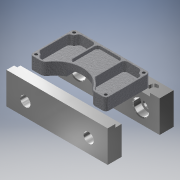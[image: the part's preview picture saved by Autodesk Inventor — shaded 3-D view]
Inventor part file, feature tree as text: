
AUTODESK INVENTOR PART (.ipt)
format: ipt  version: 2017 (Build 210142000, 142)  size: 843,264 bytes
history: native  units: in
note: dims shown in document units (in); Inventor stores cm internally (conversion verified against a paired STEP export)
features: extrude x10, sketch x9, other x5, chamfer x5, hole x3, plane x2, pattern_linear x1
ambient origin geometry x8: Origin, YZ Plane, XZ Plane, XY Plane, X Axis, Y Axis, Z Axis, Center Point
bodies: Body1 (feature_tree), Body2 (feature_tree), Body3 (feature_tree), Body4 (feature_tree), Body5 (feature_tree)
feature tree (35):
  other  "Model"
  extrude  "Extrusion1"  Depth=1.75in
  extrude  "Extrusion2"  Depth=1.075in
  sketch  "Sketch3"  dims[d5=0.125in d6=0.25in]
  extrude  "Extrusion3"  Depth=0.25in
  extrude  "Extrusion4"  Depth=0.25in
  chamfer  "Chamfer2"  Distance=0.25in
  hole  "Hole2"  [1 undecoded]
  chamfer  "Chamfer3"  Distance=0.375in
  pattern_linear  "Rectangular Pattern1"  Spacing1=1.0in  [1 undecoded]
  chamfer  "Chamfer1"  Distance=0.125in Angle=45.0deg
  plane  "Work Plane1"
  extrude  "Extrusion5"  Depth=1.5in
  plane  "Work Plane2"
  extrude  "Extrusion6"  Depth=1.5in
  extrude  "Extrusion7"  Depth=3.25in
  hole  "Hole4"  [1 undecoded]
  chamfer  "Chamfer4"  Distance=0.125in
  extrude  "Extrusion8"  Depth=0.125in
  hole  "Hole5"  [1 undecoded]
  chamfer  "Chamfer5"  Distance=0.375in
  extrude  "Extrusion9"  Depth=1.5in
  extrude  "Extrusion10"  Depth=1.5in
  sketch  "Sketch1"  dims[d0=1.75in d1=3.0in]
  sketch  "Sketch2"  dims[d3=0.5in d4=1.075in]
  sketch  "Sketch4"  dims[d7=0.5in d8=0.0in d10=1.0in d11=0.25in d12=0.0in]
  other  "Stock"
  other  "Vise Jaw - Fixed"
  sketch  "Sketch6"  dims[d13=0.063in d14=0.063in d15=0.375in d16=0.0in]
  sketch  "Sketch7"  dims[d17=0.125in d18=0.0in]
  other  "Vise Jaw"
  sketch  "Sketch8"  dims[d19=0.01in d20=0.125in d21=45.0deg]
  sketch  "Sketch9"  dims[d22=0.01in d23=0.125in d24=45.0deg]
  other  "Setup 2 - Stock"
  sketch  "Sketch10"  dims[d136=1.0in d137=1.0in d36=0.104in d37=0.25in d38=0.375in d39=0.25in d40=0.5635in d41=0.25in d42=0.0in d43=1.0in d44=1.0in d45=0.107in d46=0.25in d47=0.375in d48=0.25in d49=0.5635in d50=0.0938in d51=0.8108in d52=0.01in d53=0.125in d54=45.0deg d55=0.7874in d57=2.75in d58=0.7874in d60=1.5in d61=0.05in d62=3.25in d63=2.0in d64=0.125in d65=0.125in d66=0.75in d67=0.0in d68=0.375in d69=0.55in d70=1.25in d71=0.125in d72=0.25in d73=4.0in d74=0.0in d75=3.25in d76=0.375in d77=0.25in d78=0.14in d79=0.14in d80=0.3in d81=0.125in d82=0.0in d83=0.75in d84=2.5in d85=0.55in d86=0.4in d87=0.75in d88=0.6in d89=0.3in d90=0.5635in d91=1.0in d92=0.8108in d93=0.0312in d94=0.125in d95=45.0deg d96=1.25in d97=0.55in d100=4.0in d101=0.0in d102=0.75in d103=2.5in d104=0.55in d105=0.4in d106=0.75in d107=0.6in d108=0.3in d109=0.5635in d110=1.0in d111=0.8108in d112=0.0312in d113=0.125in d114=45.0deg d115=3.25in d116=2.0in d117=0.195in d118=0.0in d119=1.75in d120=3.0in d121=0.125in d122=0.125in d123=0.575in d124=1.075in d125=0.125in d126=0.25in d127=0.505in d128=0.0in d150=1.0in d151=1.0in d166=0.063in d167=0.0623in d168=0.063in d169=0.125in d170=0.125in d171=0.125in d172=0.1223in d173=0.1336in d174=0.1336in d175=0.125in d176=0.063in d177=0.063in d179=0.063in d180=0.071in d181=0.0751in d182=0.0713in d183=0.125in d184=1.0in d185=0.8673in d188=0.1253in d190=0.135in d191=0.125in d192=0.135in d193=0.135in d194=0.135in d195=0.135in d196=0.135in d197=0.135in d198=0.125in d199=0.135in d201=0.135in d204=0.063in d205=1.5in d206=0.135in d207=0.135in d208=0.135in d209=0.135in d210=1.5in d25=1.0in d26=1.0in d34=1.0in d35=1.0in]
note: 4 required parameter values undecoded (feature->parameter linkage not recoverable at this tier; creation-order binding heuristic only, values carry confidence <= 0.55)
